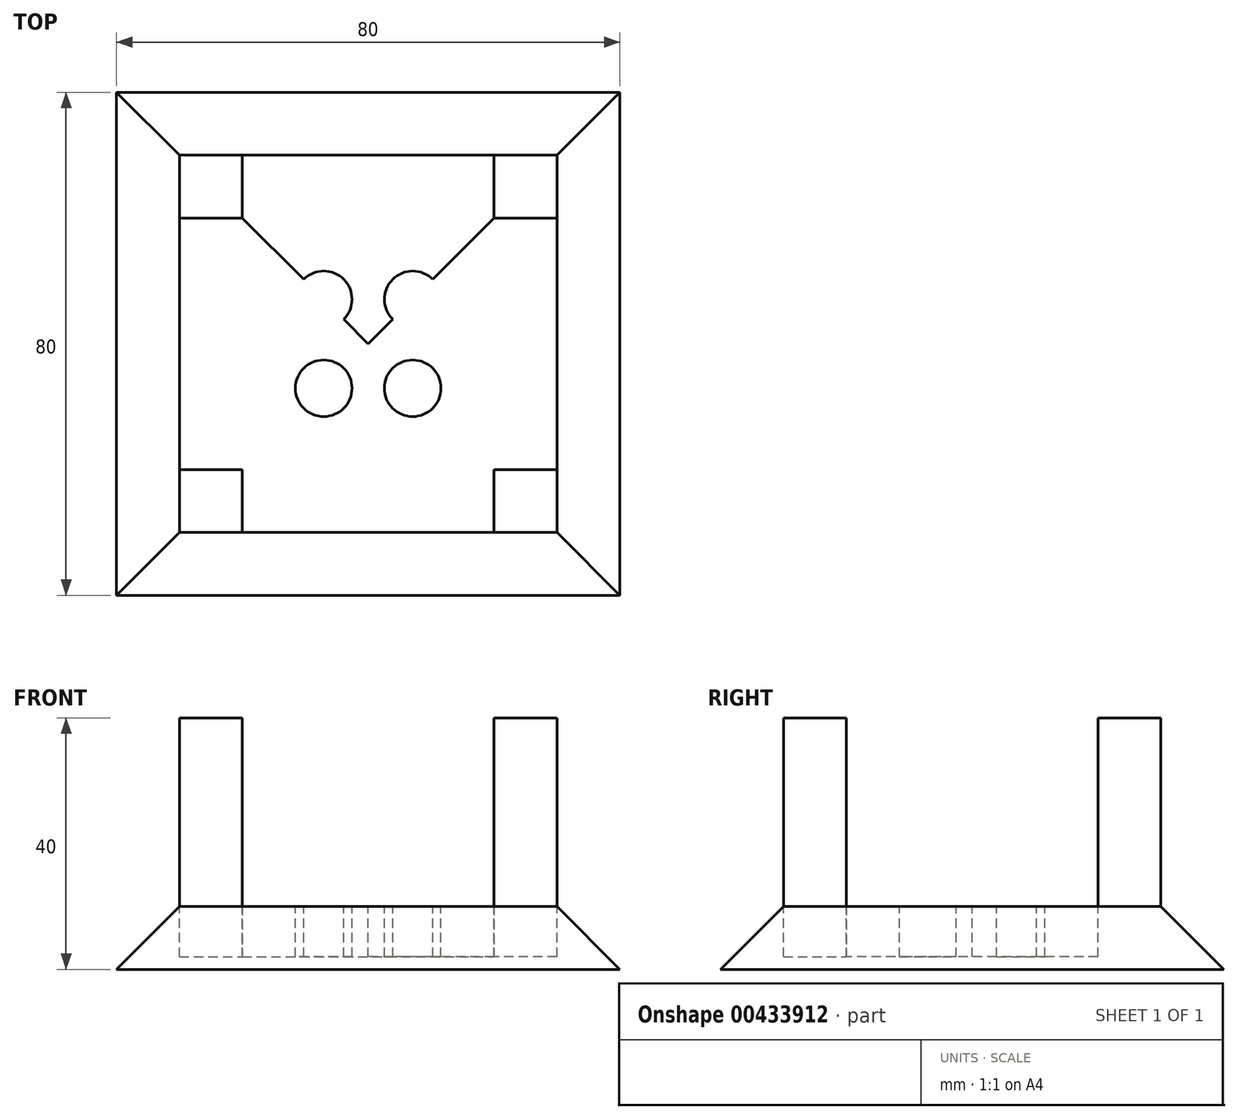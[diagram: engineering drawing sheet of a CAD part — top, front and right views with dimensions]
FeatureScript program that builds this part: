
annotation { "Feature Type Name" : "Feature", "Feature Type Description" : "" }
export const myFeature = defineFeature(function(context is Context, id is Id, definition is map)
    precondition{}
    {
        {
            var Q0;
            Q0=qCreatedBy(makeId("Top.planeOp"),FACE);
            var sketch = newSketch(context, id + "F0", { "sketchPlane" : qUnion([Q0])});
            skLineSegment(sketch, "E0.bottom", {"start": v(-40, 40) * mm, "end": v(40, 40) * mm});
            skLineSegment(sketch, "E0.top", {"start": v(-40, -40) * mm, "end": v(40, -40) * mm});
            skLineSegment(sketch, "E0.left", {"start": v(-40, 40) * mm, "end": v(-40, -40) * mm});
            skLineSegment(sketch, "E0.right", {"start": v(40, 40) * mm, "end": v(40, -40) * mm});
            skSolve(sketch);
        }
        {
            var Q0;
            Q0=makeQuery(id+"F0.imprint","IMPRINT",FACE,{"disambiguationData":[TD([[makeQuery(id+"F0.imprint","IMPRINT",EDGE,{"derivedFrom":sQuery(id+"F0.wireOp",EDGE,"E0.bottom")}),-1.0]])]});
            extrude(context, id + "F1", {"entities" : qUnion([Q0]), "depth" : 10 * mm});
        }
        {
            var Q0;
            Q0=makeQuery(id+"F1.opExtrude","CAP_FACE",FACE,{"disambiguationData":[OSD([sQuery(id+"F0.wireOp",EDGE,"E0.bottom"),sQuery(id+"F0.wireOp",EDGE,"E0.top"),sQuery(id+"F0.wireOp",EDGE,"E0.left"),sQuery(id+"F0.wireOp",EDGE,"E0.right")])],"isStart":false});
            chamfer(context, id + "F2", {"entities" : qUnion([Q0]), "chamferType" : ChamferType.OFFSET_ANGLE, "width" : 10 * mm, "oppositeDirection" : false, "angle" : 45 * degree, "tangentPropagation" : true});
        }
        {
            var Q0;
            Q0=makeQuery(id+"F1.opExtrude","CAP_FACE",FACE,{"disambiguationData":[OSD([sQuery(id+"F0.wireOp",EDGE,"E0.bottom"),sQuery(id+"F0.wireOp",EDGE,"E0.top"),sQuery(id+"F0.wireOp",EDGE,"E0.left"),sQuery(id+"F0.wireOp",EDGE,"E0.right")])],"isStart":false});
            var sketch = newSketch(context, id + "F3", { "sketchPlane" : qUnion([Q0])});
            skLineSegment(sketch, "E1.bottom", {"start": v(-30, 30) * mm, "end": v(-20, 30) * mm});
            skLineSegment(sketch, "E1.top", {"start": v(-30, 20) * mm, "end": v(-20, 20) * mm});
            skLineSegment(sketch, "E1.left", {"start": v(-30, 30) * mm, "end": v(-30, 20) * mm});
            skLineSegment(sketch, "E1.right", {"start": v(-20, 30) * mm, "end": v(-20, 20) * mm});
            skLineSegment(sketch, "E2.MirrorCS", {"start": v(30, 20) * mm, "end": v(20, 20) * mm});
            skLineSegment(sketch, "E3.MirrorCS", {"start": v(20, 30) * mm, "end": v(20, 20) * mm});
            skLineSegment(sketch, "E4.MirrorCS", {"start": v(30, 30) * mm, "end": v(20, 30) * mm});
            skLineSegment(sketch, "E5.MirrorCS", {"start": v(30, 30) * mm, "end": v(30, 20) * mm});
            skLineSegment(sketch, "E6.MirrorCS", {"start": v(-30, -20) * mm, "end": v(-20, -20) * mm});
            skLineSegment(sketch, "E7.MirrorCS", {"start": v(-20, -30) * mm, "end": v(-20, -20) * mm});
            skLineSegment(sketch, "E8.MirrorCS", {"start": v(-30, -30) * mm, "end": v(-20, -30) * mm});
            skLineSegment(sketch, "E9.MirrorCS", {"start": v(-30, -30) * mm, "end": v(-30, -20) * mm});
            skLineSegment(sketch, "E10.MirrorCS", {"start": v(20, -30) * mm, "end": v(20, -20) * mm});
            skLineSegment(sketch, "E11.MirrorCS", {"start": v(30, -20) * mm, "end": v(20, -20) * mm});
            skLineSegment(sketch, "E12.MirrorCS", {"start": v(30, -30) * mm, "end": v(30, -20) * mm});
            skLineSegment(sketch, "E13.MirrorCS", {"start": v(30, -30) * mm, "end": v(20, -30) * mm});
            skSolve(sketch);
        }
        {
            var Q0;
            Q0=makeQuery(id+"F3.imprint","IMPRINT",FACE,{"disambiguationData":[TD([[makeQuery(id+"F3.imprint","IMPRINT",EDGE,{"derivedFrom":sQuery(id+"F3.wireOp",EDGE,"E1.bottom")}),1.0]])]});
            var Q1;
            Q1=makeQuery(id+"F3.imprint","IMPRINT",FACE,{"disambiguationData":[TD([[makeQuery(id+"F3.imprint","IMPRINT",EDGE,{"derivedFrom":sQuery(id+"F3.wireOp",EDGE,"E6.MirrorCS")}),-1.0]])]});
            var Q2;
            Q2=makeQuery(id+"F3.imprint","IMPRINT",FACE,{"disambiguationData":[TD([[makeQuery(id+"F3.imprint","IMPRINT",EDGE,{"derivedFrom":sQuery(id+"F3.wireOp",EDGE,"E2.MirrorCS")}),-1.0]])]});
            var Q3;
            Q3=makeQuery(id+"F3.imprint","IMPRINT",FACE,{"disambiguationData":[TD([[makeQuery(id+"F3.imprint","IMPRINT",EDGE,{"derivedFrom":sQuery(id+"F3.wireOp",EDGE,"E10.MirrorCS")}),-1.0]])]});
            extrude(context, id + "F4", {"entities" : qUnion([Q0, Q1, Q2, Q3]), "operationType" : NewBodyOperationType.ADD, "depth" : 30 * mm});
        }
        {
            var Q0;
            Q0=makeQuery(id+"F1.opExtrude","CAP_FACE",FACE,{"disambiguationData":[OSD([sQuery(id+"F0.wireOp",EDGE,"E0.bottom"),sQuery(id+"F0.wireOp",EDGE,"E0.top"),sQuery(id+"F0.wireOp",EDGE,"E0.left"),sQuery(id+"F0.wireOp",EDGE,"E0.right")])],"isStart":false});
            var sketch = newSketch(context, id + "F5", { "sketchPlane" : qUnion([Q0])});
            skLineSegment(sketch, "E14", {"start": v(-20, 20) * mm, "end": v(20, -20) * mm});
            skLineSegment(sketch, "E15", {"start": v(20, 20) * mm, "end": v(-20, -20) * mm});
            skCircle(sketch, "E16", {"center": v(-7.07, 7.07) * mm, "radius": 4.5 * mm});
            skCircle(sketch, "E17.MirrorC", {"center": v(7.07, 7.07) * mm, "radius": 4.5 * mm});
            skCircle(sketch, "E18.MirrorC", {"center": v(-7.07, -7.07) * mm, "radius": 4.5 * mm});
            skCircle(sketch, "E19.MirrorC", {"center": v(7.07, -7.07) * mm, "radius": 4.5 * mm});
            skSolve(sketch);
        }
        {
            var Q0;
            {var subQ0=sQuery(id+"F5.wireOp",EDGE,"E16");var subQ1=sQuery(id+"F5.wireOp",EDGE,"E14");var subQ2=makeQuery(id+"F5.imprint","INTERSECT",VERTEX,{"disambiguationData":[OD(0.0)],"derivedFrom":[subQ1,subQ0]});Q0=makeQuery(id+"F5.imprint","IMPRINT",FACE,{"disambiguationData":[TD([[makeQuery(id+"F5.imprint","IMPRINT",EDGE,{"disambiguationData":[TD([[subQ2,-1.0]])],"derivedFrom":subQ1}),-1.0]])]});}
            var Q1;
            {var subQ0=sQuery(id+"F5.wireOp",EDGE,"E16");var subQ1=sQuery(id+"F5.wireOp",EDGE,"E14");var subQ2=makeQuery(id+"F5.imprint","INTERSECT",VERTEX,{"disambiguationData":[OD(0.0)],"derivedFrom":[subQ1,subQ0]});Q1=makeQuery(id+"F5.imprint","IMPRINT",FACE,{"disambiguationData":[TD([[makeQuery(id+"F5.imprint","IMPRINT",EDGE,{"disambiguationData":[TD([[subQ2,-1.0]])],"derivedFrom":subQ1}),1.0]])]});}
            var Q2;
            {var subQ0=sQuery(id+"F5.wireOp",EDGE,"E17.MirrorC");var subQ1=sQuery(id+"F5.wireOp",EDGE,"E15");var subQ2=makeQuery(id+"F5.imprint","INTERSECT",VERTEX,{"disambiguationData":[OD(0.0)],"derivedFrom":[subQ1,subQ0]});Q2=makeQuery(id+"F5.imprint","IMPRINT",FACE,{"disambiguationData":[TD([[makeQuery(id+"F5.imprint","IMPRINT",EDGE,{"disambiguationData":[TD([[subQ2,-1.0]])],"derivedFrom":subQ1}),-1.0]])]});}
            var Q3;
            {var subQ0=sQuery(id+"F5.wireOp",EDGE,"E17.MirrorC");var subQ1=sQuery(id+"F5.wireOp",EDGE,"E15");var subQ2=makeQuery(id+"F5.imprint","INTERSECT",VERTEX,{"disambiguationData":[OD(0.0)],"derivedFrom":[subQ1,subQ0]});Q3=makeQuery(id+"F5.imprint","IMPRINT",FACE,{"disambiguationData":[TD([[makeQuery(id+"F5.imprint","IMPRINT",EDGE,{"disambiguationData":[TD([[subQ2,-1.0]])],"derivedFrom":subQ1}),1.0]])]});}
            var Q4;
            {var subQ0=sQuery(id+"F5.wireOp",EDGE,"E18.MirrorC");var subQ1=sQuery(id+"F5.wireOp",EDGE,"E15");var subQ2=makeQuery(id+"F5.imprint","INTERSECT",VERTEX,{"disambiguationData":[OD(0.0)],"derivedFrom":[subQ1,subQ0]});Q4=makeQuery(id+"F5.imprint","IMPRINT",FACE,{"disambiguationData":[TD([[makeQuery(id+"F5.imprint","IMPRINT",EDGE,{"disambiguationData":[TD([[subQ2,-1.0]])],"derivedFrom":subQ1}),-1.0]])]});}
            var Q5;
            {var subQ0=sQuery(id+"F5.wireOp",EDGE,"E18.MirrorC");var subQ1=sQuery(id+"F5.wireOp",EDGE,"E15");var subQ2=makeQuery(id+"F5.imprint","INTERSECT",VERTEX,{"disambiguationData":[OD(0.0)],"derivedFrom":[subQ1,subQ0]});Q5=makeQuery(id+"F5.imprint","IMPRINT",FACE,{"disambiguationData":[TD([[makeQuery(id+"F5.imprint","IMPRINT",EDGE,{"disambiguationData":[TD([[subQ2,-1.0]])],"derivedFrom":subQ1}),1.0]])]});}
            var Q6;
            {var subQ0=sQuery(id+"F5.wireOp",EDGE,"E19.MirrorC");var subQ1=sQuery(id+"F5.wireOp",EDGE,"E14");var subQ2=makeQuery(id+"F5.imprint","INTERSECT",VERTEX,{"disambiguationData":[OD(0.0)],"derivedFrom":[subQ1,subQ0]});Q6=makeQuery(id+"F5.imprint","IMPRINT",FACE,{"disambiguationData":[TD([[makeQuery(id+"F5.imprint","IMPRINT",EDGE,{"disambiguationData":[TD([[subQ2,-1.0]])],"derivedFrom":subQ1}),-1.0]])]});}
            var Q7;
            {var subQ0=sQuery(id+"F5.wireOp",EDGE,"E19.MirrorC");var subQ1=sQuery(id+"F5.wireOp",EDGE,"E14");var subQ2=makeQuery(id+"F5.imprint","INTERSECT",VERTEX,{"disambiguationData":[OD(0.0)],"derivedFrom":[subQ1,subQ0]});Q7=makeQuery(id+"F5.imprint","IMPRINT",FACE,{"disambiguationData":[TD([[makeQuery(id+"F5.imprint","IMPRINT",EDGE,{"disambiguationData":[TD([[subQ2,-1.0]])],"derivedFrom":subQ1}),1.0]])]});}
            extrude(context, id + "F6", {"entities" : qUnion([Q0, Q1, Q2, Q3, Q4, Q5, Q6, Q7]), "operationType" : NewBodyOperationType.REMOVE, "oppositeDirection" : true, "depth" : 8 * mm});
        }
    });
